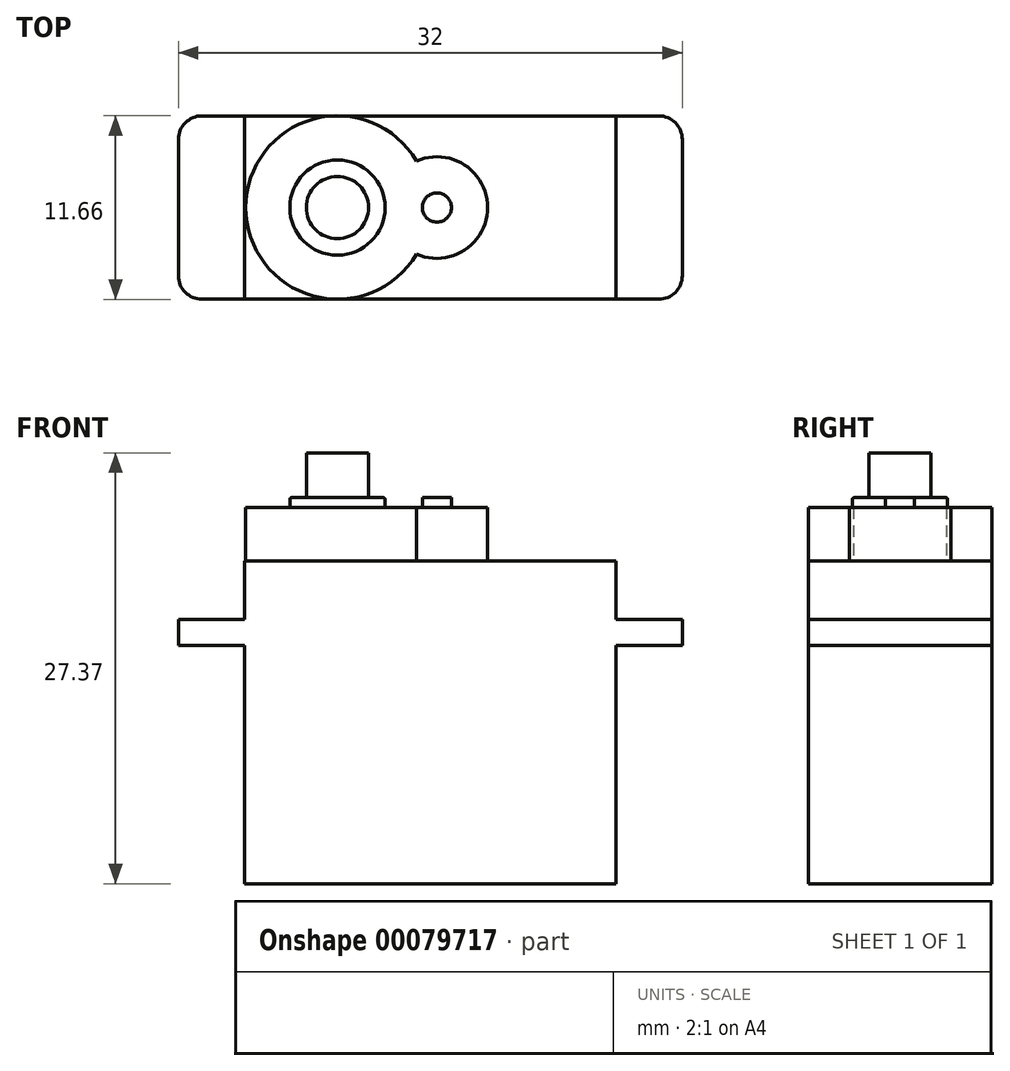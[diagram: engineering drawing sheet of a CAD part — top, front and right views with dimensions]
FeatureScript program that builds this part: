
annotation { "Feature Type Name" : "Feature", "Feature Type Description" : "" }
export const myFeature = defineFeature(function(context is Context, id is Id, definition is map)
    precondition{}
    {
        {
            var Q0;
            Q0=qCreatedBy(makeId("Top.planeOp"),FACE);
            var sketch = newSketch(context, id + "F0", { "sketchPlane" : qUnion([Q0])});
            skLineSegment(sketch, "E0.bottom", {"start": v(11.8, 5.83) * mm, "end": v(-11.8, 5.83) * mm});
            skLineSegment(sketch, "E0.top", {"start": v(11.8, -5.82) * mm, "end": v(-11.8, -5.82) * mm});
            skLineSegment(sketch, "E0.left", {"start": v(11.8, 5.83) * mm, "end": v(11.8, -5.83) * mm});
            skLineSegment(sketch, "E0.right", {"start": v(-11.8, 5.83) * mm, "end": v(-11.8, -5.82) * mm});
            skPoint(sketch, "E0.middle", {"position": v(0, 0) * mm});
            skSolve(sketch);
        }
        {
            var Q0;
            Q0 = qSketchRegion(id + "F0", true);
            extrude(context, id + "F1", {"entities" : qUnion([Q0]), "depth" : 15.15 * mm});
        }
        {
            var Q0;
            Q0=makeQuery(id+"F1.opExtrude","CAP_FACE",FACE,{"disambiguationData":[OSD([sQuery(id+"F0.wireOp",EDGE,"E0.bottom"),sQuery(id+"F0.wireOp",EDGE,"E0.top"),sQuery(id+"F0.wireOp",EDGE,"E0.left"),sQuery(id+"F0.wireOp",EDGE,"E0.right")])],"isStart":false});
            var sketch = newSketch(context, id + "F2", { "sketchPlane" : qUnion([Q0])});
            skLineSegment(sketch, "E1.bottom", {"start": v(16, 5.83) * mm, "end": v(-16, 5.83) * mm});
            skLineSegment(sketch, "E1.top", {"start": v(16, -5.83) * mm, "end": v(-16, -5.83) * mm});
            skLineSegment(sketch, "E1.left", {"start": v(16, 5.83) * mm, "end": v(16, -5.83) * mm});
            skLineSegment(sketch, "E1.right", {"start": v(-16, 5.83) * mm, "end": v(-16, -5.83) * mm});
            skPoint(sketch, "E1.middle", {"position": v(0, 0) * mm});
            skSolve(sketch);
        }
        {
            var Q0;
            Q0 = qSketchRegion(id + "F2", true);
            extrude(context, id + "F3", {"entities" : qUnion([Q0]), "operationType" : NewBodyOperationType.ADD, "depth" : 1.63 * mm});
        }
        {
            var Q0;
            Q0=makeQuery(id+"F3.opExtrude","CAP_FACE",FACE,{"disambiguationData":[OSD([sQuery(id+"F2.wireOp",EDGE,"E1.bottom"),sQuery(id+"F2.wireOp",EDGE,"E1.top"),sQuery(id+"F2.wireOp",EDGE,"E1.left"),sQuery(id+"F2.wireOp",EDGE,"E1.right")])],"isStart":false});
            var sketch = newSketch(context, id + "F4", { "sketchPlane" : qUnion([Q0])});
            skLineSegment(sketch, "E2.bottom", {"start": v(11.8, 5.83) * mm, "end": v(-11.8, 5.83) * mm});
            skLineSegment(sketch, "E2.top", {"start": v(11.8, -5.83) * mm, "end": v(-11.8, -5.83) * mm});
            skLineSegment(sketch, "E2.left", {"start": v(11.8, 5.83) * mm, "end": v(11.8, -5.83) * mm});
            skLineSegment(sketch, "E2.right", {"start": v(-11.8, 5.83) * mm, "end": v(-11.8, -5.83) * mm});
            skPoint(sketch, "E2.middle", {"position": v(0, 0) * mm});
            skSolve(sketch);
        }
        {
            var Q0;
            Q0 = qSketchRegion(id + "F4", true);
            extrude(context, id + "F5", {"entities" : qUnion([Q0]), "operationType" : NewBodyOperationType.ADD, "depth" : 3.7 * mm});
        }
        {
            var Q0;
            Q0=makeQuery(id+"F3.opExtrude","SWEPT_EDGE",EDGE,{"disambiguationData":[OSD([sQuery(id+"F2.wireOp",EDGE,"E1.top"),sQuery(id+"F2.wireOp",EDGE,"E1.right")])]});
            var Q1;
            Q1=makeQuery(id+"F3.opExtrude","SWEPT_EDGE",EDGE,{"disambiguationData":[OSD([sQuery(id+"F2.wireOp",EDGE,"E1.top"),sQuery(id+"F2.wireOp",EDGE,"E1.left")])]});
            var Q2;
            Q2=makeQuery(id+"F3.opExtrude","SWEPT_EDGE",EDGE,{"disambiguationData":[OSD([sQuery(id+"F2.wireOp",EDGE,"E1.bottom"),sQuery(id+"F2.wireOp",EDGE,"E1.left")])]});
            var Q3;
            Q3=makeQuery(id+"F3.opExtrude","SWEPT_EDGE",EDGE,{"disambiguationData":[OSD([sQuery(id+"F2.wireOp",EDGE,"E1.bottom"),sQuery(id+"F2.wireOp",EDGE,"E1.right")])]});
            fillet(context, id + "F6", {"entities" : qUnion([Q0, Q1, Q2, Q3]), "radius" : 1.5 * mm, "tangentPropagation" : true, "allowEdgeOverflow" : false});
        }
        {
            var Q0;
            Q0=makeQuery(id+"F5.opExtrude","CAP_FACE",FACE,{"disambiguationData":[OSD([sQuery(id+"F4.wireOp",EDGE,"E2.bottom"),sQuery(id+"F4.wireOp",EDGE,"E2.top"),sQuery(id+"F4.wireOp",EDGE,"E2.left"),sQuery(id+"F4.wireOp",EDGE,"E2.right")])],"isStart":false});
            var sketch = newSketch(context, id + "F7", { "sketchPlane" : qUnion([Q0])});
            skLineSegment(sketch, "E3.bottom", {"start": v(11.8, 5.83) * mm, "end": v(3.57, 5.83) * mm, "construction": true});
            skLineSegment(sketch, "E3.top", {"start": v(11.8, -5.83) * mm, "end": v(3.57, -5.83) * mm, "construction": true});
            skLineSegment(sketch, "E3.left", {"start": v(11.8, 5.83) * mm, "end": v(11.8, -5.83) * mm, "construction": true});
            skLineSegment(sketch, "E3.right", {"start": v(3.57, 5.82) * mm, "end": v(3.57, -5.83) * mm, "construction": true});
            skLineSegment(sketch, "E4", {"start": v(-11.8, 5.83) * mm, "end": v(0, -5.83) * mm, "construction": true});
            skLineSegment(sketch, "E5", {"start": v(0, 5.83) * mm, "end": v(-11.8, -5.83) * mm, "construction": true});
            skArc(sketch, "E6", {"start": v(-0.88, 2.95) * mm, "mid": v(-11.73, 0) * mm, "end": v(-0.88, -2.95) * mm});
            skArc(sketch, "E7", {"start": v(-0.88, -2.95) * mm, "mid": v(3.64, 0) * mm, "end": v(-0.88, 2.95) * mm});
            skSolve(sketch);
        }
        {
            var Q0;
            Q0 = qSketchRegion(id + "F7", true);
            extrude(context, id + "F8", {"entities" : qUnion([Q0]), "operationType" : NewBodyOperationType.ADD, "depth" : 3.42 * mm});
        }
        {
            var Q0;
            Q0=makeQuery(id+"F8.opExtrude","CAP_FACE",FACE,{"disambiguationData":[OSD([sQuery(id+"F7.wireOp",EDGE,"E6"),sQuery(id+"F7.wireOp",EDGE,"E7")])],"isStart":false});
            var sketch = newSketch(context, id + "F9", { "sketchPlane" : qUnion([Q0])});
            skCircle(sketch, "E8", {"center": v(0.42, 0) * mm, "radius": 0.93 * mm});
            skCircle(sketch, "E9", {"center": v(-5.9, 0) * mm, "radius": 3.02 * mm});
            skSolve(sketch);
        }
        {
            var Q0;
            Q0=makeQuery(id+"F9.imprint","IMPRINT",FACE,{"disambiguationData":[TD([[makeQuery(id+"F9.imprint","IMPRINT",EDGE,{"derivedFrom":sQuery(id+"F9.wireOp",EDGE,"E8")}),1.0]])]});
            var Q1;
            Q1=makeQuery(id+"F9.imprint","IMPRINT",FACE,{"disambiguationData":[TD([[makeQuery(id+"F9.imprint","IMPRINT",EDGE,{"derivedFrom":sQuery(id+"F9.wireOp",EDGE,"E9")}),1.0]])]});
            extrude(context, id + "F10", {"entities" : qUnion([Q0, Q1]), "operationType" : NewBodyOperationType.ADD, "depth" : .61 * mm});
        }
        {
            var Q0;
            Q0=makeQuery(id+"F10.opExtrude","CAP_EDGE",EDGE,{"disambiguationData":[OSD([sQuery(id+"F9.wireOp",EDGE,"E9")])],"isStart":false});
            fillet(context, id + "F11", {"entities" : qUnion([Q0]), "radius" : .1 * mm, "tangentPropagation" : true, "allowEdgeOverflow" : false});
        }
        {
            var Q0;
            Q0=makeQuery(id+"F10.opExtrude","CAP_FACE",FACE,{"disambiguationData":[OSD([sQuery(id+"F9.wireOp",EDGE,"E9")])],"isStart":false});
            var sketch = newSketch(context, id + "F12", { "sketchPlane" : qUnion([Q0])});
            skCircle(sketch, "E10", {"center": v(-5.9, 0) * mm, "radius": 1.98 * mm});
            skSolve(sketch);
        }
        {
            var Q0;
            Q0 = qSketchRegion(id + "F12", true);
            extrude(context, id + "F13", {"entities" : qUnion([Q0]), "operationType" : NewBodyOperationType.ADD, "depth" : 2.85 * mm});
        }
    });
